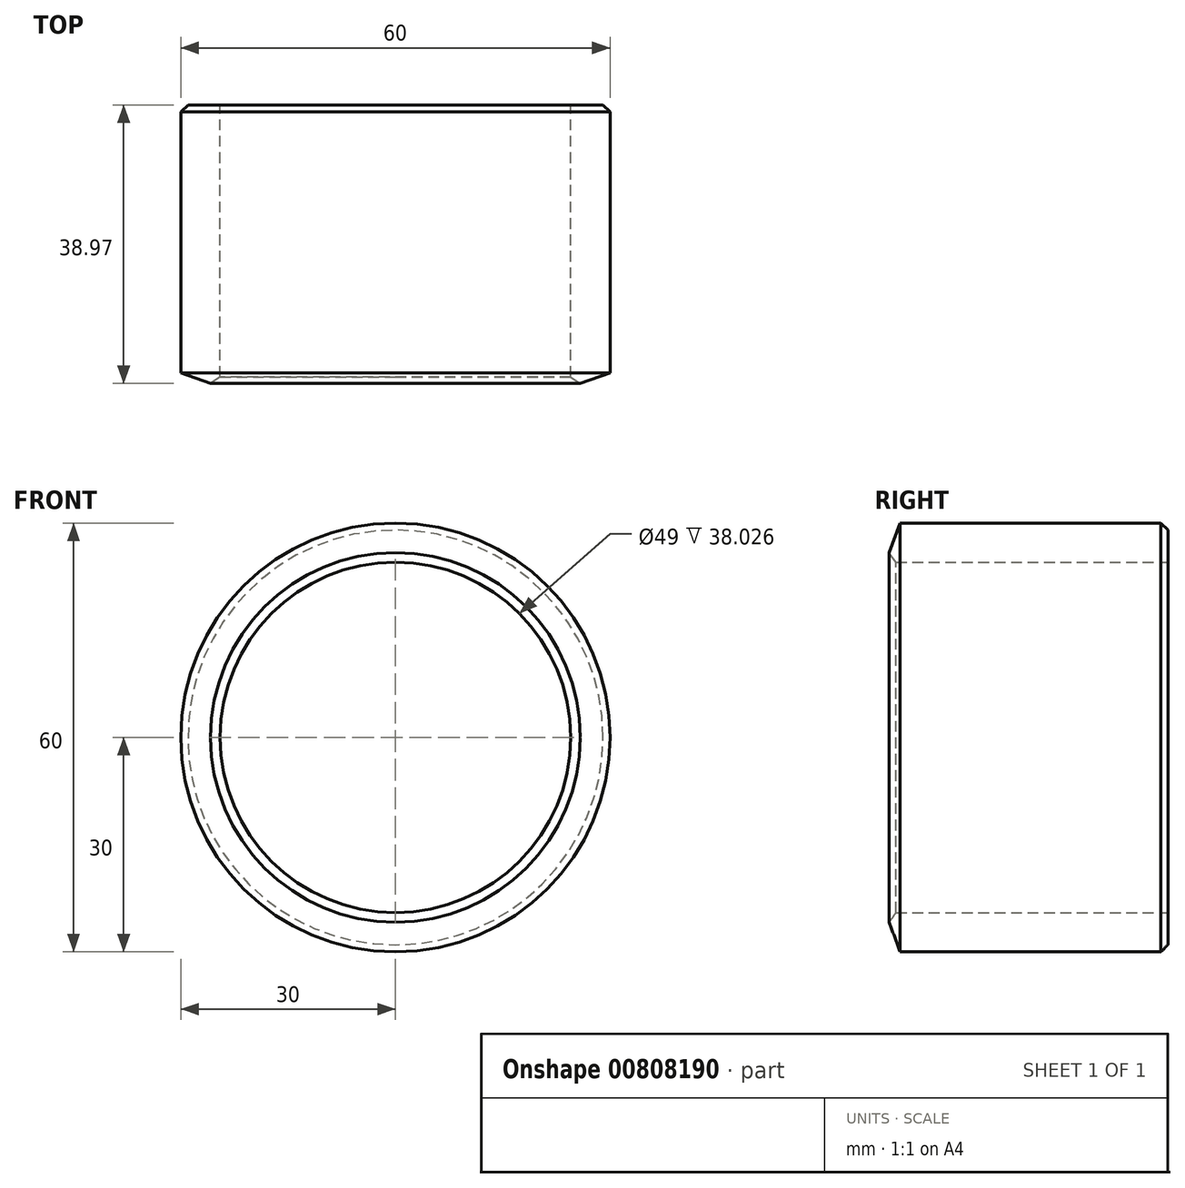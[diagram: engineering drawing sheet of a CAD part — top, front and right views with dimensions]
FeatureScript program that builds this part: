
annotation { "Feature Type Name" : "Feature", "Feature Type Description" : "" }
export const myFeature = defineFeature(function(context is Context, id is Id, definition is map)
    precondition{}
    {
        {
            var Q0;
            Q0=qCreatedBy(makeId("Front.planeOp"),FACE);
            var sketch = newSketch(context, id + "F0", { "sketchPlane" : qUnion([Q0])});
            skCircle(sketch, "E0", {"center": v(0, 0) * mm, "radius": 30 * mm});
            skCircle(sketch, "E1", {"center": v(0, 0) * mm, "radius": 24.5 * mm});
            skSolve(sketch);
        }
        {
            var Q0;
            Q0 = qSketchRegion(id + "F0", true);
            extrude(context, id + "F1", {"entities" : qUnion([Q0]), "depth" : 40 * mm, "offsetDistance" : 25 * mm});
        }
        {
            var Q0;
            Q0=makeQuery(id+"F1.opExtrude","CAP_EDGE",EDGE,{"disambiguationData":[OSD([sQuery(id+"F0.wireOp",EDGE,"E0")])],"isStart":false});
            chamfer(context, id + "F2", {"entities" : qUnion([Q0]), "chamferType" : ChamferType.OFFSET_ANGLE, "width" : 7 * mm, "oppositeDirection" : false, "angle" : 20 * degree, "tangentPropagation" : true});
        }
        {
            var Q0;
            Q0=makeQuery(id+"F2.opChamfer","BLEND_EDGE",EDGE,{"blendedFrom":[makeQuery(id+"F1.opExtrude","CAP_EDGE",EDGE,{"disambiguationData":[OSD([sQuery(id+"F0.wireOp",EDGE,"E0")])],"isStart":false}),makeQuery(id+"F1.opExtrude","SWEPT_FACE",FACE,{"disambiguationData":[OSD([sQuery(id+"F0.wireOp",EDGE,"E1")])]})],"blendedInto":[makeQuery(id+"F1.opExtrude","SWEPT_FACE",FACE,{"disambiguationData":[OSD([sQuery(id+"F0.wireOp",EDGE,"E1")])]})]});
            var Q1;
            Q1=makeQuery(id+"F1.opExtrude","CAP_EDGE",EDGE,{"disambiguationData":[OSD([sQuery(id+"F0.wireOp",EDGE,"E0")])],"isStart":true});
            chamfer(context, id + "F3", {"entities" : qUnion([Q0, Q1]), "width" : 1 * mm, "tangentPropagation" : true});
        }
    });
